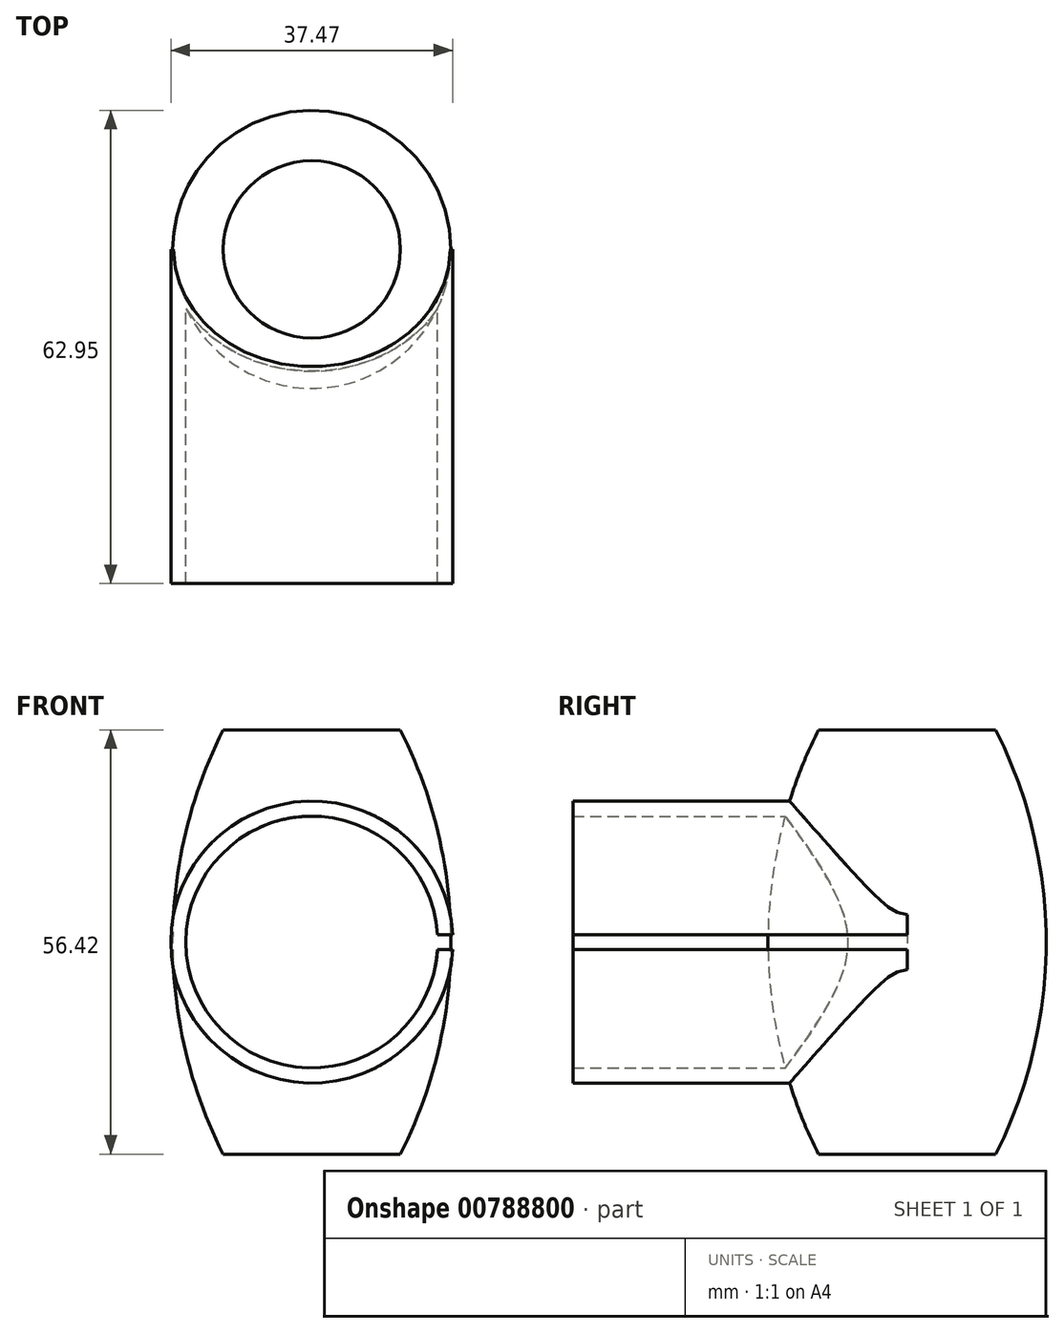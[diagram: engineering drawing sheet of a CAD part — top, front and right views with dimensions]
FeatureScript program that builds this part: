
annotation { "Feature Type Name" : "Feature", "Feature Type Description" : "" }
export const myFeature = defineFeature(function(context is Context, id is Id, definition is map)
    precondition{}
    {
        {
            var Q0;
            Q0=qCreatedBy(makeId("Front.planeOp"),FACE);
            var sketch = newSketch(context, id + "F0", { "sketchPlane" : qUnion([Q0])});
            skArc(sketch, "E0", {"start": v(16.72, 1) * mm, "mid": v(-16.75, 0) * mm, "end": v(16.72, -1) * mm});
            skArc(sketch, "E1.0", {"start": v(18.72, 1) * mm, "mid": v(-18.75, 0) * mm, "end": v(18.72, -1) * mm});
            skLineSegment(sketch, "E2", {"start": v(0, 0) * mm, "end": v(18.75, 0) * mm, "construction": true});
            skLineSegment(sketch, "E3.0", {"start": v(16.72, -1) * mm, "end": v(18.72, -1) * mm});
            skLineSegment(sketch, "E4.0", {"start": v(16.72, 1) * mm, "end": v(18.72, 1) * mm});
            skSolve(sketch);
        }
        {
            var Q0;
            Q0 = qSketchRegion(id + "F0", true);
            extrude(context, id + "F1", {"entities" : qUnion([Q0]), "depth" : 44.45 * mm, "offsetDistance" : 25.4 * mm});
        }
        {
            var Q0;
            Q0=qCreatedBy(makeId("Right.planeOp"),FACE);
            var sketch = newSketch(context, id + "F2", { "sketchPlane" : qUnion([Q0])});
            skLineSegment(sketch, "E5", {"start": v(0, 0) * mm, "end": v(0, 28.21) * mm});
            skLineSegment(sketch, "E6", {"start": v(0, 0) * mm, "end": v(0, -28.21) * mm});
            skLineSegment(sketch, "E7", {"start": v(0, 0) * mm, "end": v(18.5, 0) * mm, "construction": true});
            skLineSegment(sketch, "E8", {"start": v(0, 0) * mm, "end": v(0, 44.45) * mm, "construction": true});
            skLineSegment(sketch, "E9", {"start": v(0, 0) * mm, "end": v(0, -44.45) * mm, "construction": true});
            skArc(sketch, "E10", {"start": v(11.79, -28.21) * mm, "mid": v(18.5, 0) * mm, "end": v(11.79, 28.21) * mm});
            skLineSegment(sketch, "E11", {"start": v(0, 28.21) * mm, "end": v(11.79, 28.21) * mm});
            skLineSegment(sketch, "E12", {"start": v(0, -28.21) * mm, "end": v(11.79, -28.21) * mm});
            skSolve(sketch);
        }
        {
            var Q0;
            Q0=makeQuery(id+"F2.imprint","IMPRINT",FACE,{"disambiguationData":[TD([[makeQuery(id+"F2.imprint","IMPRINT",EDGE,{"derivedFrom":sQuery(id+"F2.wireOp",EDGE,"E5")}),-1.0]])]});
            var Q1;
            Q1 = qConstructionFilter(qBodyType(qCreatedBy(id + "F2" ,EDGE), BodyType.WIRE), ConstructionObject.NO);
            var Q2;
            Q2=sQuery(id+"F2.wireOp",EDGE,"E5");
            revolve(context, id + "F3", {"operationType" : NewBodyOperationType.ADD, "surfaceOperationType" : NewSurfaceOperationType.ADD, "entities" : qUnion([Q0]), "surfaceEntities" : qUnion([Q1]), "axis" : qUnion([Q2]), "revolveType" : RevolveType.FULL});
        }
    });
